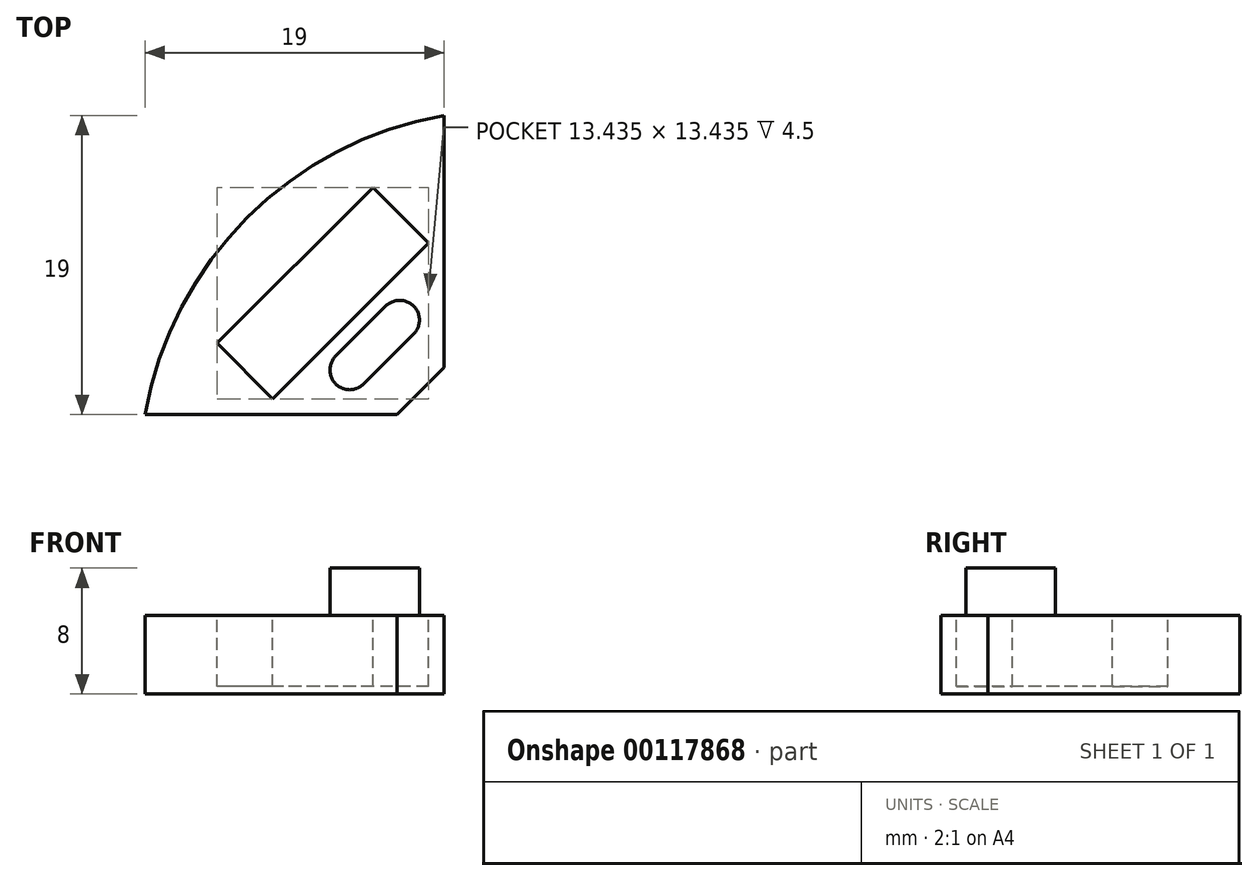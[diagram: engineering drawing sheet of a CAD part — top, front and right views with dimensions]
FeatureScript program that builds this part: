
annotation { "Feature Type Name" : "Feature", "Feature Type Description" : "" }
export const myFeature = defineFeature(function(context is Context, id is Id, definition is map)
    precondition{}
    {
        {
            var Q0;
            Q0=qCreatedBy(makeId("Top.planeOp"),FACE);
            var sketch = newSketch(context, id + "F0", { "sketchPlane" : qUnion([Q0])});
            skLineSegment(sketch, "E0", {"start": v(0, 3) * mm, "end": v(0, 19) * mm});
            skLineSegment(sketch, "E1", {"start": v(-3, 0) * mm, "end": v(-19, 0) * mm});
            skArc(sketch, "E2", {"start": v(0, 19) * mm, "mid": v(-12.51, 12.51) * mm, "end": v(-19, 0) * mm});
            skPoint(sketch, "E3.visualSharp", {"position": v(0, 0) * mm});
            skLineSegment(sketch, "E4", {"start": v(-3, 0) * mm, "end": v(0, 3) * mm});
            skSolve(sketch);
        }
        {
            var Q0;
            Q0=makeQuery(id+"F0.imprint","IMPRINT",FACE,{"disambiguationData":[TD([[makeQuery(id+"F0.imprint","IMPRINT",EDGE,{"derivedFrom":sQuery(id+"F0.wireOp",EDGE,"E0")}),1.0]])]});
            extrude(context, id + "F1", {"entities" : qUnion([Q0]), "depth" : 5 * mm});
        }
        {
            var Q0;
            Q0=makeQuery(id+"F1.opExtrude","CAP_FACE",FACE,{"disambiguationData":[OSD([sQuery(id+"F0.wireOp",EDGE,"E0"),sQuery(id+"F0.wireOp",EDGE,"E1"),sQuery(id+"F0.wireOp",EDGE,"E2"),sQuery(id+"F0.wireOp",EDGE,"E3.filletArc")])],"isStart":false});
            var sketch = newSketch(context, id + "F2", { "sketchPlane" : qUnion([Q0])});
            skLineSegment(sketch, "E5.bottom", {"start": v(-1, 10.9) * mm, "end": v(-10.9, 1) * mm});
            skLineSegment(sketch, "E5.top", {"start": v(-4.54, 14.44) * mm, "end": v(-14.44, 4.54) * mm});
            skLineSegment(sketch, "E5.left", {"start": v(-1, 10.9) * mm, "end": v(-4.54, 14.44) * mm});
            skLineSegment(sketch, "E5.right", {"start": v(-10.9, 1) * mm, "end": v(-14.44, 4.54) * mm});
            skSolve(sketch);
        }
        {
            var Q0;
            Q0=makeQuery(id+"F2.imprint","IMPRINT",FACE,{"disambiguationData":[TD([[makeQuery(id+"F2.imprint","IMPRINT",EDGE,{"derivedFrom":sQuery(id+"F2.wireOp",EDGE,"E5.bottom")}),-1.0]])]});
            extrude(context, id + "F3", {"entities" : qUnion([Q0]), "operationType" : NewBodyOperationType.REMOVE, "oppositeDirection" : true, "depth" : 4.5 * mm});
        }
        {
            var Q0;
            Q0=makeQuery(id+"F2.imprint","IMPRINT",FACE,{"disambiguationData":[TD([[makeQuery(id+"F2.imprint","IMPRINT",EDGE,{"derivedFrom":sQuery(id+"F2.wireOp",EDGE,"E5.bottom")}),1.0]])]});
            var sketch = newSketch(context, id + "F4", { "sketchPlane" : qUnion([Q0])});
            skLineSegment(sketch, "E6", {"start": v(-6.9, 3.71) * mm, "end": v(-3.71, 6.9) * mm});
            skLineSegment(sketch, "E7", {"start": v(-1.94, 5.13) * mm, "end": v(-5.13, 1.94) * mm});
            skArc(sketch, "E8", {"start": v(-6.9, 3.71) * mm, "mid": v(-6.9, 1.94) * mm, "end": v(-5.13, 1.94) * mm});
            skArc(sketch, "E9", {"start": v(-1.94, 5.13) * mm, "mid": v(-1.95, 6.9) * mm, "end": v(-3.71, 6.9) * mm});
            skLineSegment(sketch, "E10", {"start": v(-3.54, 3.54) * mm, "end": v(3.35, -3.35) * mm, "construction": true});
            skSolve(sketch);
        }
        {
            var Q0;
            Q0=qSketchRegion(id+"F4",true);
            extrude(context, id + "F5", {"entities" : qUnion([Q0]), "operationType" : NewBodyOperationType.ADD, "depth" : 3 * mm});
        }
    });
